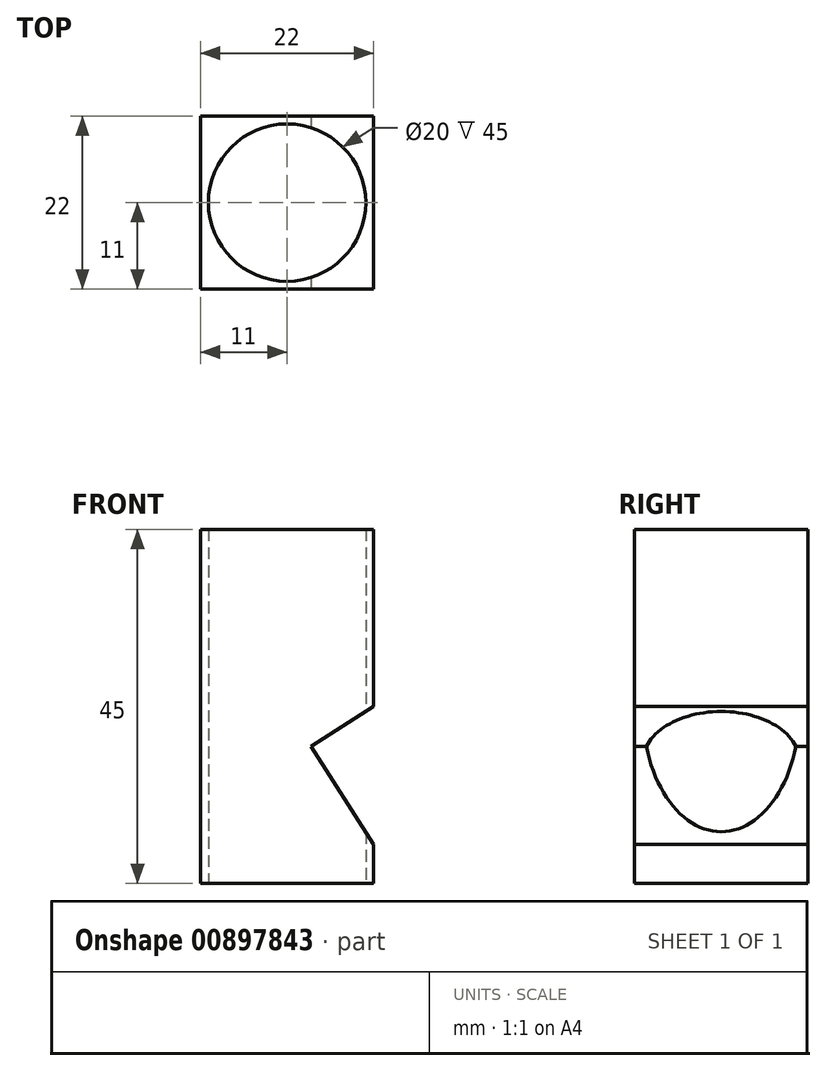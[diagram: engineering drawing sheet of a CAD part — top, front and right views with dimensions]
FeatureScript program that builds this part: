
annotation { "Feature Type Name" : "Feature", "Feature Type Description" : "" }
export const myFeature = defineFeature(function(context is Context, id is Id, definition is map)
    precondition{}
    {
        {
            var Q0;
            Q0=qCreatedBy(makeId("Top.planeOp"),FACE);
            var sketch = newSketch(context, id + "F0", { "sketchPlane" : qUnion([Q0])});
            skLineSegment(sketch, "E0.bottom", {"start": v(11, 11) * mm, "end": v(-11, 11) * mm});
            skLineSegment(sketch, "E0.top", {"start": v(11, -11) * mm, "end": v(-11, -11) * mm});
            skLineSegment(sketch, "E0.left", {"start": v(11, 11) * mm, "end": v(11, -11) * mm});
            skLineSegment(sketch, "E0.right", {"start": v(-11, 11) * mm, "end": v(-11, -11) * mm});
            skPoint(sketch, "E0.middle", {"position": v(0, 0) * mm});
            skCircle(sketch, "E1", {"center": v(0, 0) * mm, "radius": 10 * mm});
            skSolve(sketch);
        }
        {
            var Q0;
            Q0=makeQuery(id+"F0.imprint","IMPRINT",FACE,{"disambiguationData":[TD([[makeQuery(id+"F0.imprint","IMPRINT",EDGE,{"derivedFrom":sQuery(id+"F0.wireOp",EDGE,"E0.bottom")}),1.0]])]});
            extrude(context, id + "F1", {"entities" : qUnion([Q0]), "depth" : 45 * mm, "offsetDistance" : 25.4 * mm});
        }
        {
            var Q0;
            Q0=makeQuery(id+"F1.opExtrude","SWEPT_FACE",FACE,{"disambiguationData":[OSD([sQuery(id+"F0.wireOp",EDGE,"E0.top")])]});
            var sketch = newSketch(context, id + "F2", { "sketchPlane" : qUnion([Q0])});
            skLineSegment(sketch, "E2", {"start": v(11, 22.5) * mm, "end": v(3.05, 17.41) * mm});
            skLineSegment(sketch, "E3", {"start": v(3.05, 17.41) * mm, "end": v(11, 5) * mm});
            skLineSegment(sketch, "E4", {"start": v(11, 5) * mm, "end": v(11, 22.5) * mm});
            skSolve(sketch);
        }
        {
            var Q0;
            Q0=makeQuery(id+"F2.imprint","IMPRINT",FACE,{"disambiguationData":[TD([[makeQuery(id+"F2.imprint","IMPRINT",EDGE,{"derivedFrom":sQuery(id+"F2.wireOp",EDGE,"E2")}),1.0]])]});
            var Q1;
            Q1=sQuery(id+"F2.wireOp",EDGE,"E2");
            var Q2;
            Q2=sQuery(id+"F2.wireOp",EDGE,"E3");
            var Q3;
            Q3=sQuery(id+"F2.wireOp",EDGE,"E4");
            extrude(context, id + "F3", {"entities" : qUnion([Q0]), "operationType" : NewBodyOperationType.REMOVE, "surfaceEntities" : qUnion([Q1, Q2, Q3]), "endBound" : BoundingType.THROUGH_ALL, "oppositeDirection" : true, "depth" : 0 * mm, "offsetDistance" : 25 * mm});
        }
    });
